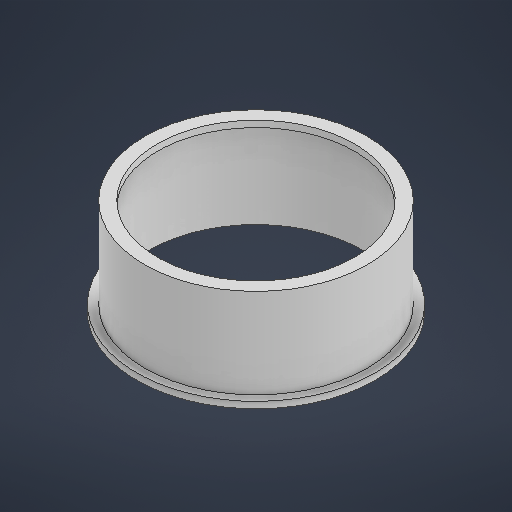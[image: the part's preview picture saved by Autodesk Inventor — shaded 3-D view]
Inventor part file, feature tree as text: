
AUTODESK INVENTOR PART (.ipt)
format: ipt  version: 2025 (Build 290162000, 162)  size: 285,696 bytes
history: native  units: in
note: dims shown in document units (in); Inventor stores cm internally (conversion verified against a paired STEP export)
features: other x12, sketch x9, extrude x6, plane x1
ambient origin geometry x8: Origin, YZ Plane, XZ Plane, XY Plane, X Axis, Y Axis, Z Axis, Center Point
bodies: Solid1 (feature_tree)
feature tree (28):
  other  "Table"
  other  "C .Replace - 01"
  other  "C .Replace - 02"
  other  "C .Replace - 03"
  other  "C .Replace - 04"
  other  "C .Replace - 05"
  other  "C .Replace - 06"
  other  "C .Replace - 07"
  other  "C .Replace - 08"
  other  "C .Replace - 09"
  other  "C .Replace - 10"
  other  "C .Replace - Face"
  sketch  "Sketch1"  dims[d5=0.0in d7=0.0in]
  extrude  "Extrusion1"  TaperAngle=0.0deg  [1 undecoded]
  extrude  "Extrusion2"  Depth=10.0394in
  sketch  "Sketch2"  dims[d28=0.1969in d29=3.937in d31=360.0deg]
  extrude  "Extrusion7"  Depth=3.937in TaperAngle=360.0deg
  plane  "Work Plane2"
  extrude  "Extrusion8"  Depth=0.3937in
  extrude  "Extrusion30"  Depth=0.2165in
  sketch  "Sketch25"  dims[d240=2.3622in d242=360.0deg]
  extrude  "Extrusion31"  Depth=0.3937in TaperAngle=0.0deg
  sketch  "Sketch3"  dims[d33=0.3937in d34=0.0in d52=4.5276in]
  sketch  "Sketch Circular Pattern1"  dims[d18=0.0in d27=10.0394in]
  sketch  "Sketch24"  dims[d239=0.2559in]
  sketch  "Sketch Circular Pattern4"  dims[d230=4.0157in d231=0.2165in]
  sketch  "Sketch26"  dims[d244=0.1969in d245=0.0in d113=0.0197in d114=0.0344in d115=0.0197in d116=0.0344in d167=0.0197in d168=0.0344in d169=0.0197in d170=0.0344in d215=0.0197in d216=0.0344in d217=0.0197in d218=0.0344in d219=0.0in d220=0.0in]
  sketch  "Sketch Circular Pattern5"  dims[d232=2.3622in d234=360.0deg d236=0.3937in d237=0.0in]
note: 1 required parameter value undecoded (feature->parameter linkage not recoverable at this tier; creation-order binding heuristic only, values carry confidence <= 0.55)
